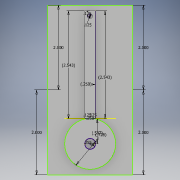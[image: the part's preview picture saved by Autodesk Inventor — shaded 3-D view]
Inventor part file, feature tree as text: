
AUTODESK INVENTOR PART (.ipt)
format: ipt  version: 2017 (Build 210142000, 142)  size: 155,136 bytes
history: native  units: in
note: dims shown in document units (in); Inventor stores cm internally (conversion verified against a paired STEP export)
features: sketch x9, extrude x5, hole x2, plane x1
ambient origin geometry x8: Origin, YZ Plane, XZ Plane, XY Plane, X Axis, Y Axis, Z Axis, Center Point
bodies: Solid1 (feature_tree)
feature tree (17):
  extrude  "Extrusion1"  Depth=0.125in
  sketch  "Sketch2"  dims[d1=0.125in d2=0.0in d3=0.125in]
  plane  "Work Plane1"
  extrude  "Extrusion2"  Depth=0.25in
  extrude  "Extrusion3"  Depth=0.5in TaperAngle=0.0deg
  sketch  "Sketch6"  dims[d24=0.255in]
  hole  "Hole1"  [1 undecoded]
  hole  "Hole2"  [1 undecoded]
  extrude  "Extrusion6"  Depth=2.0in
  extrude  "Extrusion7"  Depth=2.0in
  sketch  "Sketch9"  dims[d40=0.125in d41=1.0in d42=0.0in]
  sketch  "Sketch10"  dims[d45=2.0in d46=2.0in]
  sketch  "Sketch11"  dims[d47=2.0in d48=2.0in d49=0.125in d50=0.0in d51=2.5427in d52=2.5427in d53=0.7275in d54=0.25in d55=0.5868in]
  sketch  "Sketch3"  dims[d4=0.125in d6=0.25in]
  sketch  "Sketch4"  dims[d7=2.5295in d8=0.0in d9=0.5in d10=0.0in]
  sketch  "Sketch7"  dims[d25=0.255in d26=0.75in d27=0.375in d28=0.25in d29=0.5635in d30=1.0in d31=0.8108in]
  sketch  "Sketch8"  dims[d32=0.255in d33=0.75in d34=0.375in d35=0.25in d36=0.5635in d37=0.3125in d38=0.8108in d39=0.125in]
note: 2 required parameter values undecoded (feature->parameter linkage not recoverable at this tier; creation-order binding heuristic only, values carry confidence <= 0.55)
